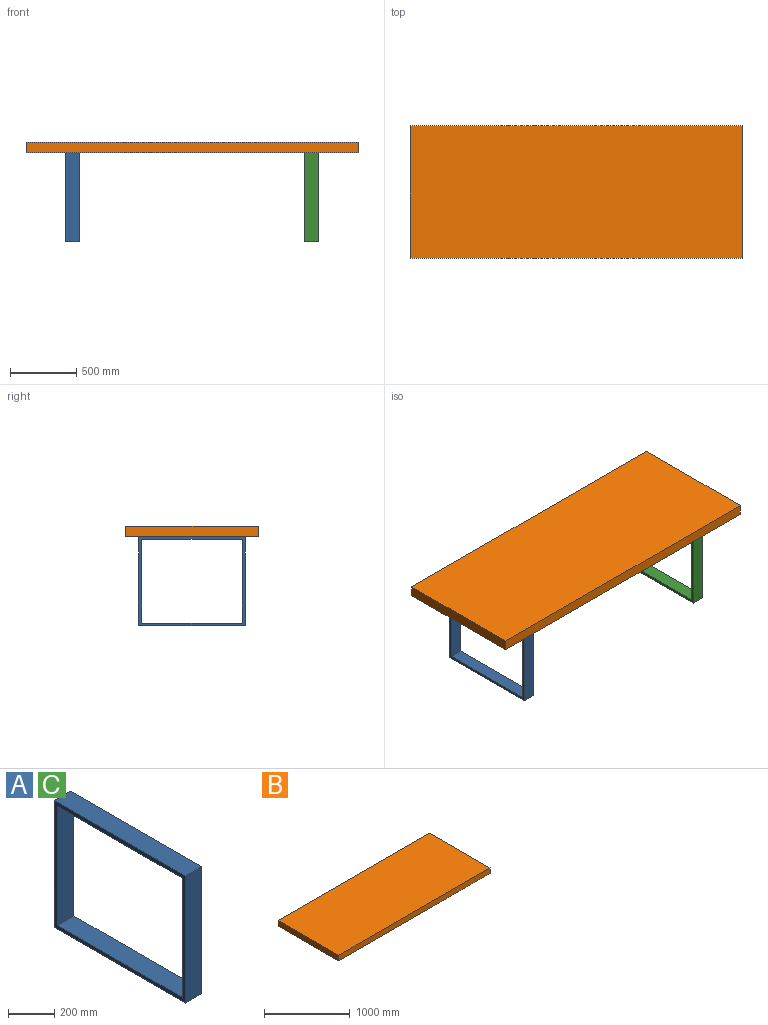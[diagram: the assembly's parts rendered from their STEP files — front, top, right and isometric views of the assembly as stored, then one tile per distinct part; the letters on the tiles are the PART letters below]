
ASSEMBLY  parts=3 mates=2
PART A: 10 faces, bbox 100x800x670 mm
  f0: plane 670x100mm, normal (0,1,0), area 67000mm2, adj f1,f7,f8,f9
  f1: plane 800x100mm, normal (0,0,1), area 80000mm2, adj f0,f2,f8,f9
  f2: plane 670x100mm, normal (0,-1,0), area 67000mm2, adj f1,f7,f8,f9
  f3: plane 630x100mm, normal (0,-1,0), area 63000mm2, adj f4,f6,f8,f9
  f4: plane 760x100mm, normal (0,0,1), area 76000mm2, adj f3,f5,f8,f9
  f5: plane 630x100mm, normal (0,1,0), area 63000mm2, adj f4,f6,f8,f9
  f6: plane 760x100mm, normal (0,0,-1), area 76000mm2, adj f3,f5,f8,f9
  f7: plane 800x100mm, normal (0,0,-1), area 80000mm2, adj f0,f2,f8,f9
  f8: plane 800x670mm, normal (1,0,0), area 57200mm2, adj f0,f1,f2,f3,f4,f5,f6,f7
  f9: plane 800x670mm, normal (-1,0,0), area 57200mm2, adj f0,f1,f2,f3,f4,f5,f6,f7
PART B: 6 faces, bbox 2500x1000x80 mm
  f0: plane 2500x80mm, normal (0,-1,0), area 200000mm2, adj f1,f3,f4,f5
  f1: plane 1000x80mm, normal (1,0,0), area 80000mm2, adj f0,f2,f4,f5
  f2: plane 2500x80mm, normal (0,1,0), area 200000mm2, adj f1,f3,f4,f5
  f3: plane 1000x80mm, normal (-1,0,0), area 80000mm2, adj f0,f2,f4,f5
  f4: plane 2500x1000mm, normal (0,0,1), area 2500000mm2, adj f0,f1,f2,f3
  f5: plane 2500x1000mm, normal (0,0,-1), area 2500000mm2, adj f0,f1,f2,f3
PART C: same geometry as A
PLACE A t=(-1080,0,-382)mm
PLACE B rot(axis=(-1,0,0),180deg) t=(-130,0,33)mm
PLACE C t=(720,0,-382)mm
MATE fastened C.f1 <-> B.f4  axis (0,0,1) through (770,0,-47)mm
MATE fastened A.f1 <-> B.f4  axis (0,0,1) through (-1030,0,-47)mm
